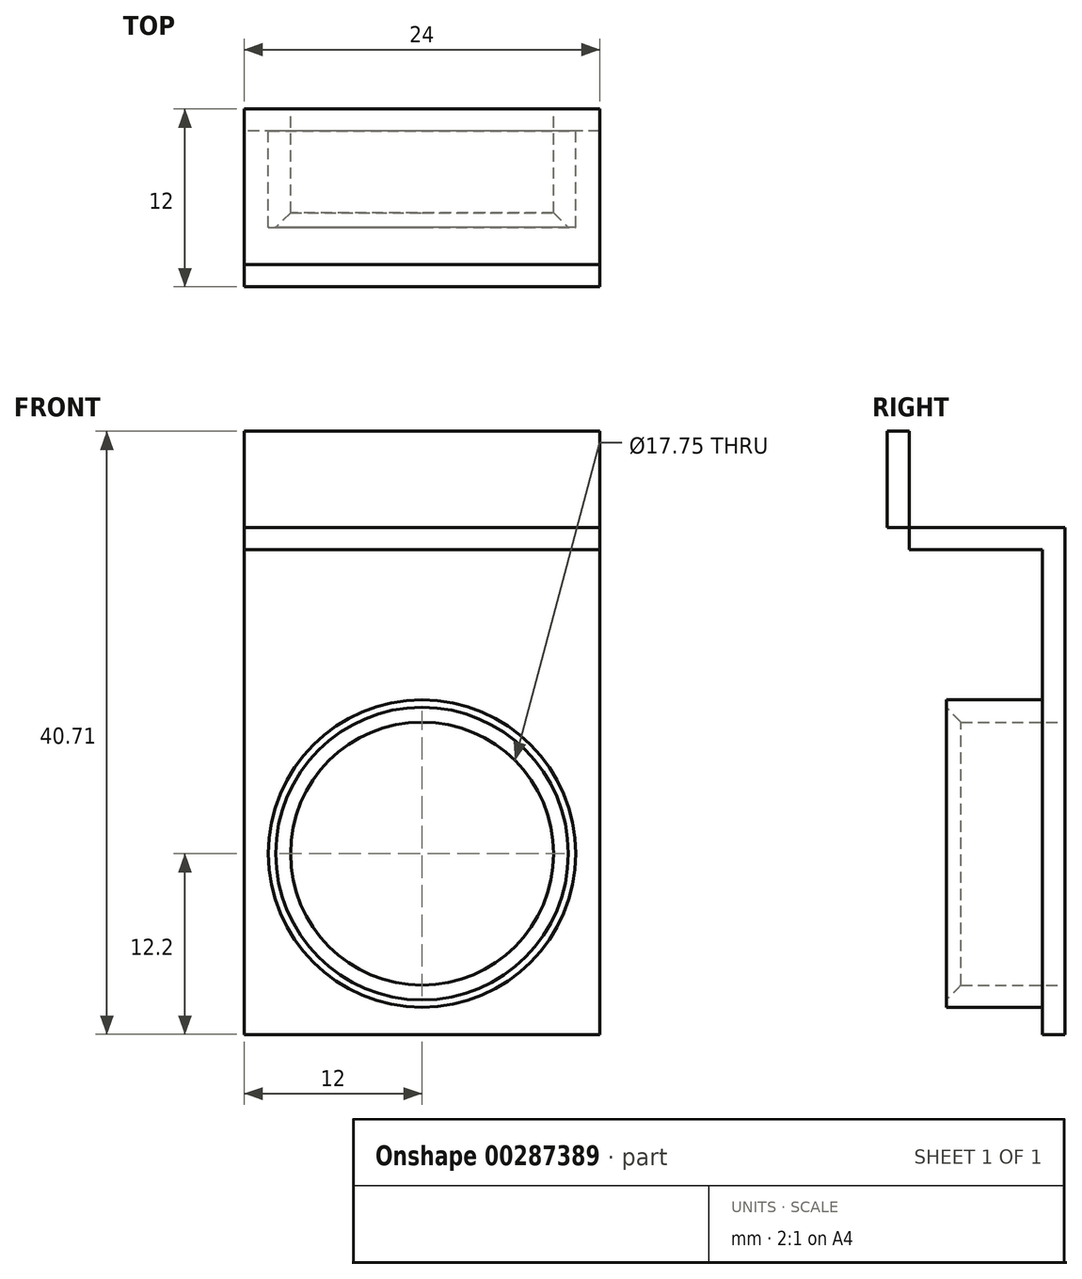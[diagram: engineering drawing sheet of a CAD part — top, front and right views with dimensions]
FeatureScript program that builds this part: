
annotation { "Feature Type Name" : "Feature", "Feature Type Description" : "" }
export const myFeature = defineFeature(function(context is Context, id is Id, definition is map)
    precondition{}
    {
        {
            var Q0;
            Q0=qCreatedBy(makeId("Front.planeOp"),FACE);
            var sketch = newSketch(context, id + "F0", { "sketchPlane" : qUnion([Q0])});
            skCircle(sketch, "E0", {"center": v(0, 0) * mm, "radius": 8.88 * mm});
            skCircle(sketch, "E1.0", {"center": v(0, 0) * mm, "radius": 10.38 * mm});
            skSolve(sketch);
        }
        {
            var Q0;
            Q0=qCreatedBy(makeId("Right.planeOp"),FACE);
            var sketch = newSketch(context, id + "F1", { "sketchPlane" : qUnion([Q0])});
            skLineSegment(sketch, "E2.bottom", {"start": v(0, -12.2) * mm, "end": v(-1.5, -12.2) * mm});
            skLineSegment(sketch, "E2.top", {"start": v(0, 22) * mm, "end": v(-1.5, 22) * mm});
            skLineSegment(sketch, "E2.left", {"start": v(0, -12.2) * mm, "end": v(0, 22) * mm});
            skLineSegment(sketch, "E2.right", {"start": v(-1.5, -12.2) * mm, "end": v(-1.5, 20.5) * mm});
            skLineSegment(sketch, "E3.bottom", {"start": v(0, 22) * mm, "end": v(-12, 22) * mm});
            skLineSegment(sketch, "E3.top", {"start": v(-1.5, 20.5) * mm, "end": v(-12, 20.5) * mm});
            skLineSegment(sketch, "E3.left", {"start": v(0, 22) * mm, "end": v(0, 20.5) * mm});
            skLineSegment(sketch, "E3.right", {"start": v(-12, 22) * mm, "end": v(-12, 20.5) * mm});
            skLineSegment(sketch, "E4.bottom", {"start": v(-12, 20.5) * mm, "end": v(-10.5, 20.5) * mm});
            skLineSegment(sketch, "E4.top", {"start": v(-12, 28.5) * mm, "end": v(-10.5, 28.5) * mm});
            skLineSegment(sketch, "E4.left", {"start": v(-12, 20.5) * mm, "end": v(-12, 28.5) * mm});
            skLineSegment(sketch, "E4.right", {"start": v(-10.5, 20.5) * mm, "end": v(-10.5, 28.5) * mm});
            skSolve(sketch);
        }
        {
            var Q0;
            Q0=makeQuery(id+"F1.imprint","IMPRINT",FACE,{"disambiguationData":[TD([[makeQuery(id+"F1.imprint","IMPRINT",EDGE,{"derivedFrom":sQuery(id+"F1.wireOp",EDGE,"E2.bottom")}),-1.0]])]});
            var Q1;
            {var subQ5=sQuery(id+"F1.wireOp",EDGE,"E4.top");Q1=makeQuery(id+"F1.imprint","IMPRINT",FACE,{"disambiguationData":[TD([[makeQuery(id+"F1.imprint","IMPRINT",EDGE,{"derivedFrom":subQ5}),-1.0]])]});}
            var Q2;
            {var subQ5=sQuery(id+"F1.wireOp",EDGE,"E4.bottom");Q2=makeQuery(id+"F1.imprint","IMPRINT",FACE,{"disambiguationData":[TD([[makeQuery(id+"F1.imprint","IMPRINT",EDGE,{"derivedFrom":subQ5}),1.0]])]});}
            extrude(context, id + "F2", {"entities" : qUnion([Q0, Q1, Q2]), "depth" : 12 * mm, "hasSecondDirection" : true, "secondDirectionOppositeDirection" : true, "secondDirectionDepth" : 12 * mm});
        }
        {
            var Q0;
            Q0=makeQuery(id+"F0.imprint","IMPRINT",FACE,{"disambiguationData":[TD([[makeQuery(id+"F0.imprint","IMPRINT",EDGE,{"derivedFrom":sQuery(id+"F0.wireOp",EDGE,"E0")}),1.0]])]});
            extrude(context, id + "F3", {"entities" : qUnion([Q0]), "operationType" : NewBodyOperationType.REMOVE, "depth" : 25 * mm});
        }
        {
            var Q0;
            Q0=makeQuery(id+"F0.imprint","IMPRINT",FACE,{"disambiguationData":[TD([[makeQuery(id+"F0.imprint","IMPRINT",EDGE,{"derivedFrom":sQuery(id+"F0.wireOp",EDGE,"E0")}),-1.0]])]});
            extrude(context, id + "F4", {"entities" : qUnion([Q0]), "operationType" : NewBodyOperationType.ADD, "depth" : 8 * mm});
        }
        {
            var Q0;
            Q0=makeQuery(id+"F4.opExtrude","CAP_EDGE",EDGE,{"disambiguationData":[OSD([sQuery(id+"F0.wireOp",EDGE,"E0")])],"isStart":false});
            var Q1;
            Q1=makeQuery(id+"F3.boolean.opBoolean","COPY",EDGE,{"derivedFrom":makeQuery(id+"F3.opExtrude","CAP_EDGE",EDGE,{"disambiguationData":[OSD([sQuery(id+"F0.wireOp",EDGE,"E0")])],"isStart":true})});
            chamfer(context, id + "F5", {"entities" : qUnion([Q0, Q1]), "width" : 1 * mm, "tangentPropagation" : true});
        }
    });
